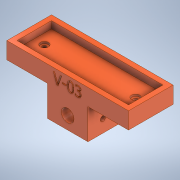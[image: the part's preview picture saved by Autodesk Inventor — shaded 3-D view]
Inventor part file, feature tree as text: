
AUTODESK INVENTOR PART (.ipt)
format: ipt  version: 2021.1 (Build 251245010, 245A)  size: 306,176 bytes
history: native  units: in
note: dims shown in document units (in); Inventor stores cm internally (conversion verified against a paired STEP export)
features: sketch x8, extrude x5, hole x4, projected_geometry x1
ambient origin geometry x8: Origin, YZ Plane, XZ Plane, XY Plane, X Axis, Y Axis, Z Axis, Center Point
bodies: Solid1 (feature_tree)
feature tree (18):
  sketch  "Sketch1"  dims[d0=1.7in d1=5.5in]
  extrude  "Extrusion1"  Depth=5.5in
  extrude  "Extrusion2"  Depth=0.25in
  hole  "Hole1"  [1 undecoded]
  extrude  "Extrusion6"  TaperAngle=0.0deg  [1 undecoded]
  extrude  "Extrusion7"  Depth=0.5in
  hole  "Hole2"  [1 undecoded]
  hole  "Hole3"  [1 undecoded]
  hole  "Hole4"  [1 undecoded]
  extrude  "Extrusion8"  TaperAngle=0.0deg  [1 undecoded]
  sketch  "Sketch2"  dims[d2=0.25in d3=0.25in]
  sketch  "Sketch5"  dims[d4=0.475in d5=0.0in]
  sketch  "Sketch6"  dims[d6=0.35in d7=0.0in]
  projected_geometry  "Projected Loop1"
  sketch  "Sketch7"  dims[d8=0.5in d9=0.5in]
  sketch  "Sketch9"  dims[d10=0.201in d11=0.75in d12=0.4in d13=0.1in d14=0.5635in d15=1.0in d16=0.8108in d17=0.625in]
  sketch  "Sketch10"  dims[d24=0.625in d27=2.0in]
  sketch  "Sketch11"  dims[d28=2.2in d29=1.5in d30=0.0in d31=0.625in d32=0.5in d33=0.0in d34=0.625in d35=1.0in d36=0.7333in d37=0.7874in d39=0.7333in d40=0.3937in d42=1.0in d44=0.201in d45=0.75in d46=0.257in d47=0.25in d48=0.5635in d49=1.0in d50=0.8108in d60=0.625in d61=0.7333in d62=0.7874in d64=0.7333in d65=0.3937in d67=1.0in d69=0.201in d70=0.75in d71=0.257in d72=0.375in d73=0.5635in d74=1.0in d75=0.8108in d76=0.625in d77=0.201in d78=0.75in d79=0.257in d80=0.375in d81=0.5635in d82=1.0in d83=0.8108in d84=0.1in d85=0.0in]
note: 6 required parameter values undecoded (feature->parameter linkage not recoverable at this tier; creation-order binding heuristic only, values carry confidence <= 0.55)
